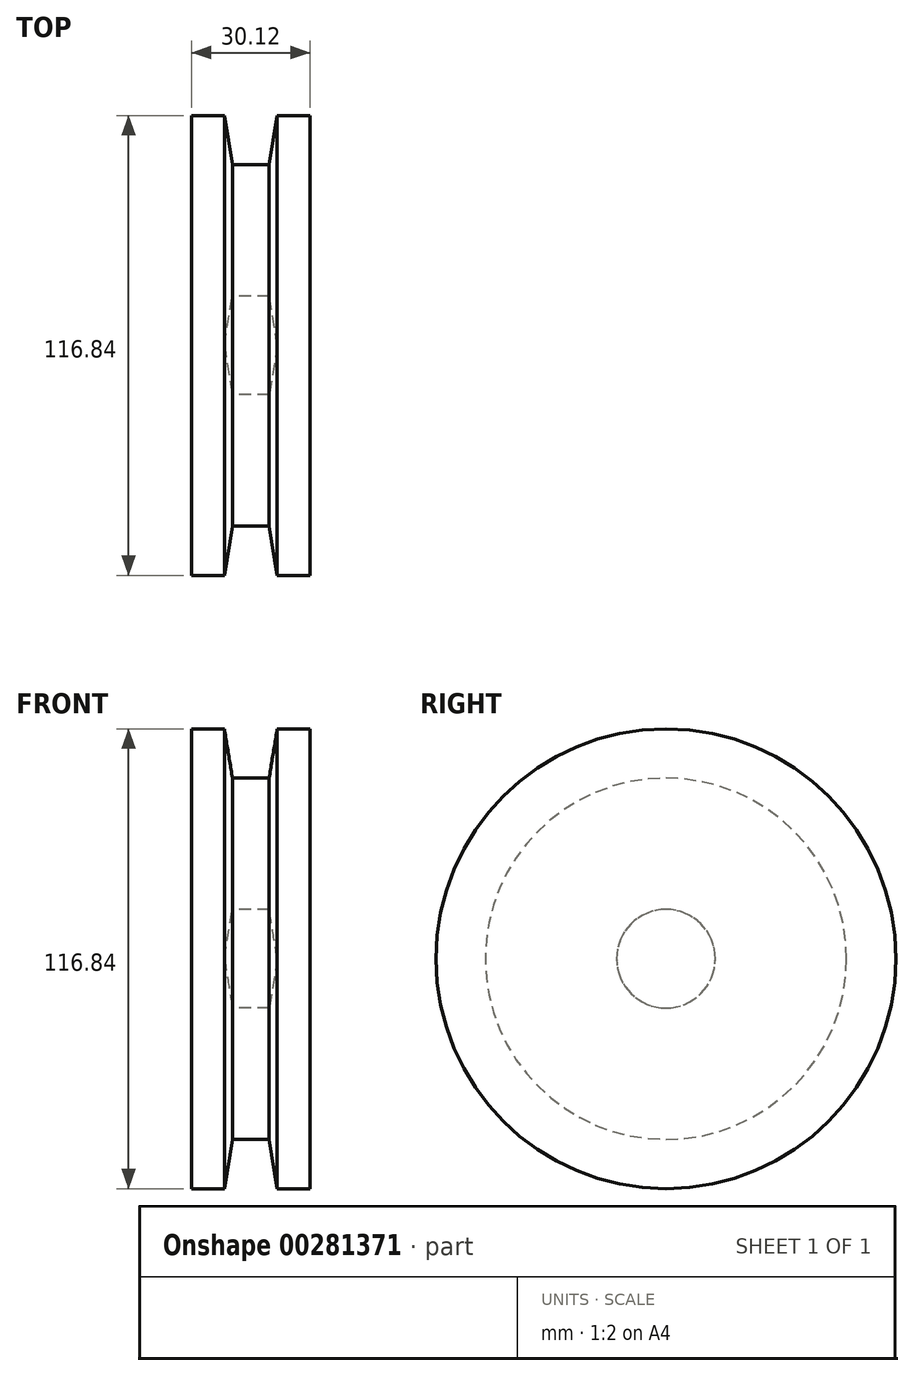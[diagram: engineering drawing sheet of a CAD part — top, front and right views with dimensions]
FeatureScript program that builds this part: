
annotation { "Feature Type Name" : "Feature", "Feature Type Description" : "" }
export const myFeature = defineFeature(function(context is Context, id is Id, definition is map)
    precondition{}
    {
        {
            var Q0;
            Q0=qCreatedBy(makeId("Front.planeOp"),FACE);
            var sketch = newSketch(context, id + "F0", { "sketchPlane" : qUnion([Q0])});
            skLineSegment(sketch, "E0", {"start": v(-15.06, 29.21) * mm, "end": v(-15.06, 0) * mm});
            skLineSegment(sketch, "E1", {"start": v(-15.06, 29.21) * mm, "end": v(-6.73, 29.21) * mm});
            skLineSegment(sketch, "E2", {"start": v(-6.73, 29.21) * mm, "end": v(-4.66, 16.68) * mm});
            skLineSegment(sketch, "E3", {"start": v(-4.66, 16.68) * mm, "end": v(0, 16.68) * mm});
            skLineSegment(sketch, "E4.MirrorCS", {"start": v(4.66, 16.68) * mm, "end": v(0, 16.68) * mm});
            skLineSegment(sketch, "E5.MirrorCS", {"start": v(6.73, 29.21) * mm, "end": v(4.66, 16.68) * mm});
            skLineSegment(sketch, "E6.MirrorCS", {"start": v(15.06, 29.21) * mm, "end": v(6.73, 29.21) * mm});
            skLineSegment(sketch, "E7.MirrorCS", {"start": v(15.06, 29.21) * mm, "end": v(15.06, 0) * mm});
            skLineSegment(sketch, "E8.MirrorCS", {"start": v(-15.06, -29.21) * mm, "end": v(-15.06, 0) * mm});
            skLineSegment(sketch, "E9.MirrorCS", {"start": v(-15.06, -29.21) * mm, "end": v(-6.73, -29.21) * mm});
            skLineSegment(sketch, "E10.MirrorCS", {"start": v(-6.73, -29.21) * mm, "end": v(-4.66, -16.68) * mm});
            skLineSegment(sketch, "E11.MirrorCS", {"start": v(-4.66, -16.68) * mm, "end": v(0, -16.68) * mm});
            skLineSegment(sketch, "E12.MirrorCS", {"start": v(4.66, -16.68) * mm, "end": v(0, -16.68) * mm});
            skLineSegment(sketch, "E13.MirrorCS", {"start": v(6.73, -29.21) * mm, "end": v(4.66, -16.68) * mm});
            skLineSegment(sketch, "E14.MirrorCS", {"start": v(15.06, -29.21) * mm, "end": v(6.73, -29.21) * mm});
            skLineSegment(sketch, "E15.MirrorCS", {"start": v(15.06, -29.21) * mm, "end": v(15.06, 0) * mm});
            skSolve(sketch);
        }
        {
            var Q0;
            Q0=makeQuery(id+"F0.imprint","IMPRINT",FACE,{"disambiguationData":[TD([[makeQuery(id+"F0.imprint","IMPRINT",EDGE,{"derivedFrom":sQuery(id+"F0.wireOp",EDGE,"E0")}),1.0]])]});
            var Q1;
            Q1=sQuery(id+"F0.wireOp",EDGE,"E9.MirrorCS");
            revolve(context, id + "F1", {"entities" : qUnion([Q0]), "axis" : qUnion([Q1]), "revolveType" : RevolveType.FULL});
        }
    });
